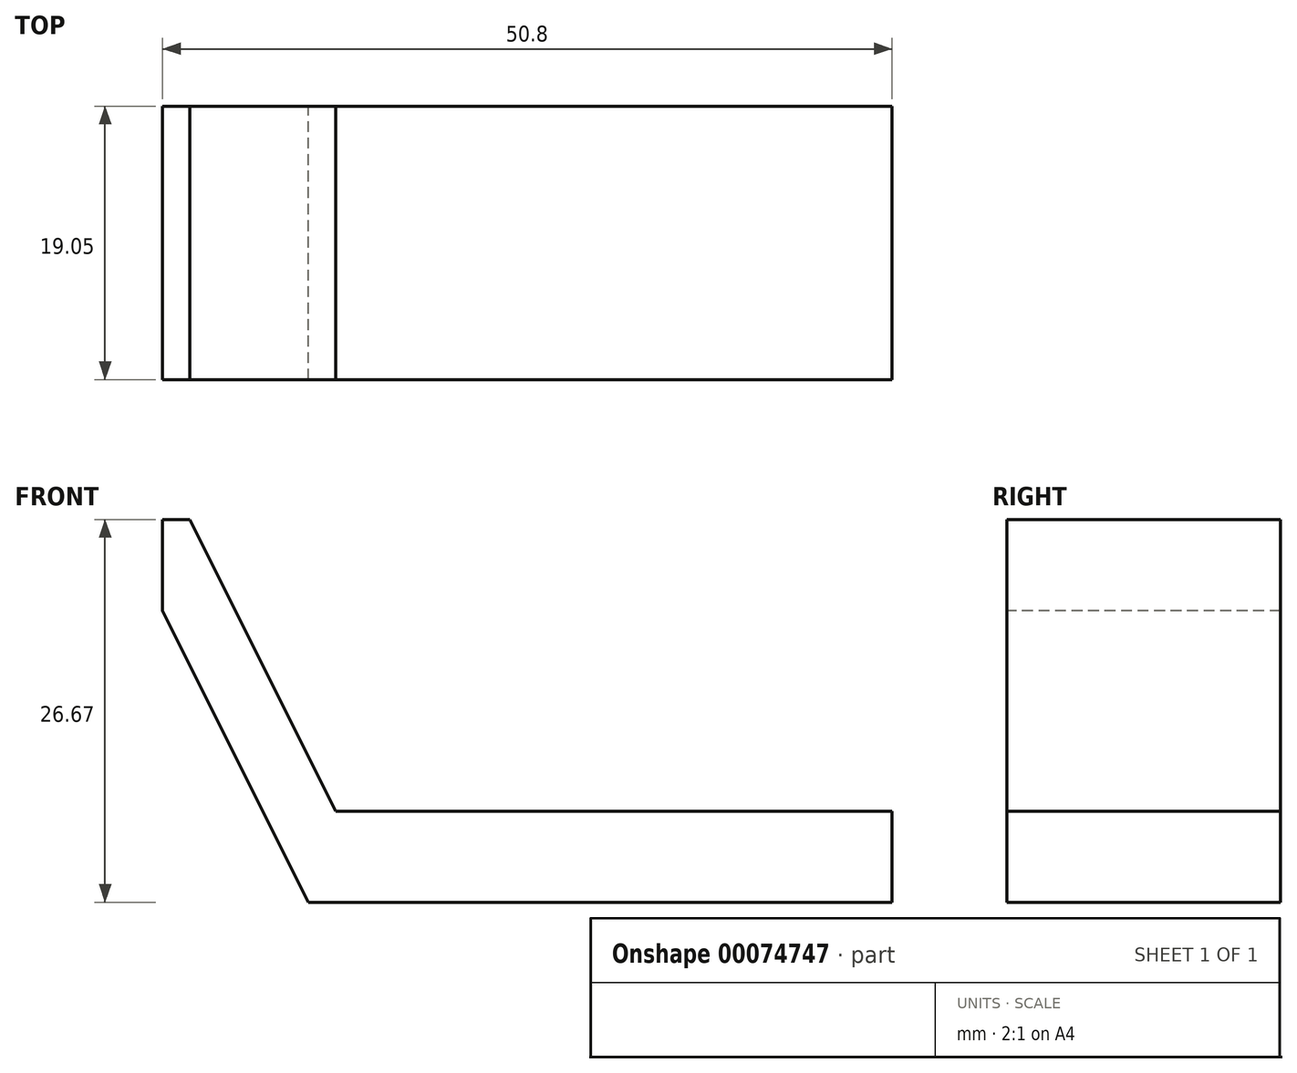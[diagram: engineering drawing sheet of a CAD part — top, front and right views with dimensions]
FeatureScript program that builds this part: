
annotation { "Feature Type Name" : "Feature", "Feature Type Description" : "" }
export const myFeature = defineFeature(function(context is Context, id is Id, definition is map)
    precondition{}
    {
        {
            var Q0;
            Q0=qCreatedBy(makeId("Front.planeOp"),FACE);
            var sketch = newSketch(context, id + "F0", { "sketchPlane" : qUnion([Q0])});
            skLineSegment(sketch, "E0", {"start": v(0, 0) * mm, "end": v(-50.8, 0) * mm});
            skLineSegment(sketch, "E1", {"start": v(-50.8, 0) * mm, "end": v(-50.8, -6.35) * mm});
            skLineSegment(sketch, "E2", {"start": v(-50.8, -6.35) * mm, "end": v(0, -6.35) * mm});
            skLineSegment(sketch, "E3", {"start": v(0, 0) * mm, "end": v(0, -6.35) * mm});
            skSolve(sketch);
        }
        {
            var Q0;
            Q0 = qSketchRegion(id + "F0", true);
            extrude(context, id + "F1", {"entities" : qUnion([Q0]), "depth" : 19.05 * mm});
        }
        {
            var Q0;
            Q0=makeQuery(id+"F1.opExtrude","SWEPT_FACE",FACE,{"disambiguationData":[OSD([sQuery(id+"F0.wireOp",EDGE,"E0")])]});
            var sketch = newSketch(context, id + "F2", { "sketchPlane" : qUnion([Q0])});
            skLineSegment(sketch, "E4", {"start": v(-38.74, 0) * mm, "end": v(-38.74, -19.05) * mm});
            skSolve(sketch);
        }
        {
            var Q0;
            {var subQ0=sQuery(id+"F2.wireOp",EDGE,"E4");Q0=makeQuery(id+"F2.imprint","IMPRINT",FACE,{"disambiguationData":[TD([[makeQuery(id+"F2.imprint","IMPRINT",EDGE,{"derivedFrom":subQ0}),-1.0]])]});}
            extrude(context, id + "F3", {"entities" : qUnion([Q0]), "operationType" : NewBodyOperationType.ADD, "depth" : 20.32 * mm});
        }
        {
            var Q0;
            Q0=makeQuery(id+"F3.opExtrude","CAP_EDGE",EDGE,{"disambiguationData":[OSD([sQuery(id+"F2.wireOp",EDGE,"E4")])],"isStart":false});
            chamfer(context, id + "F4", {"entities" : qUnion([Q0]), "chamferType" : ChamferType.TWO_OFFSETS, "width1" : 20.32 * mm, "oppositeDirection" : false, "width2" : 10.16 * mm, "tangentPropagation" : true});
        }
        {
            var Q0;
            Q0=makeQuery(id+"F1.opExtrude","SWEPT_EDGE",EDGE,{"disambiguationData":[OSD([sQuery(id+"F0.wireOp",EDGE,"E1"),sQuery(id+"F0.wireOp",EDGE,"E2")])]});
            chamfer(context, id + "F5", {"entities" : qUnion([Q0]), "chamferType" : ChamferType.TWO_OFFSETS, "width1" : 10.16 * mm, "oppositeDirection" : false, "width2" : 20.32 * mm, "tangentPropagation" : true});
        }
    });
